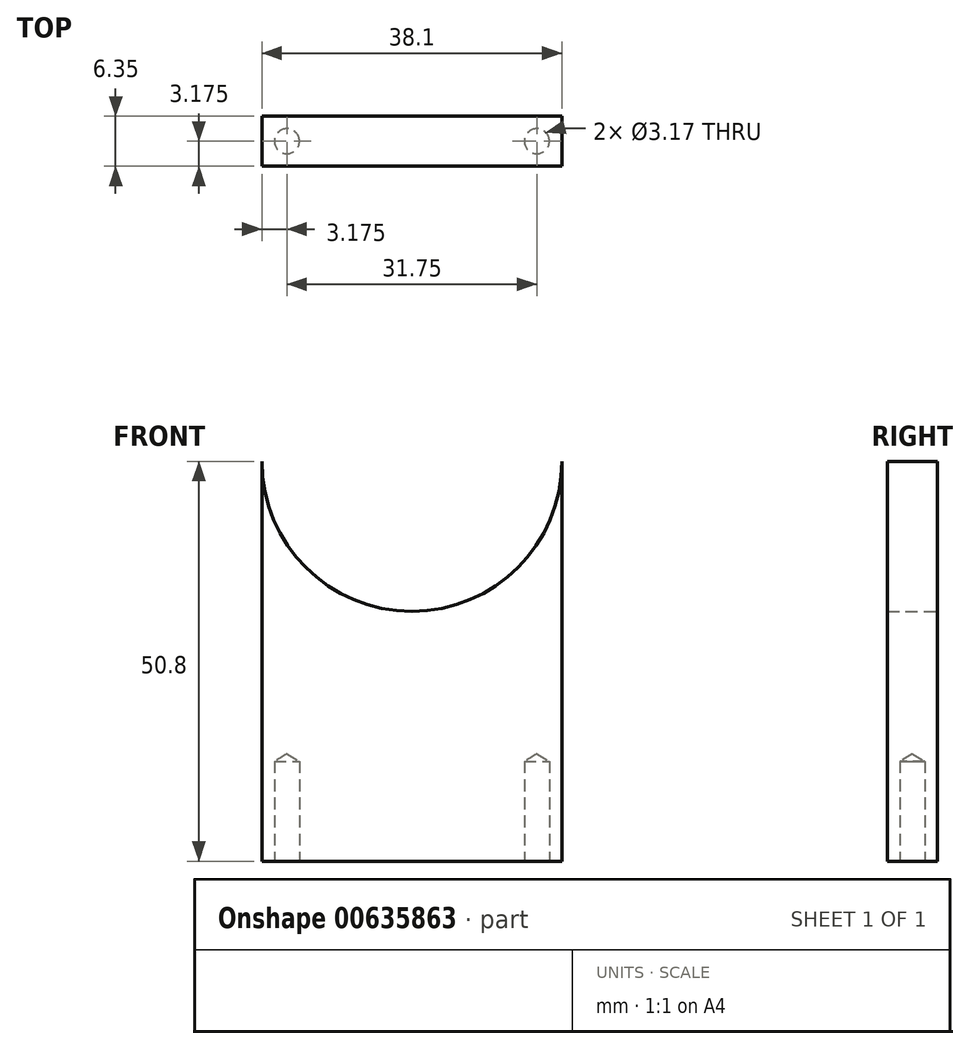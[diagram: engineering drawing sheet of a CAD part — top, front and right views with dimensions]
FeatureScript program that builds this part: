
annotation { "Feature Type Name" : "Feature", "Feature Type Description" : "" }
export const myFeature = defineFeature(function(context is Context, id is Id, definition is map)
    precondition{}
    {
        {
            var Q0;
            Q0=qCreatedBy(makeId("Front.planeOp"),FACE);
            var sketch = newSketch(context, id + "F0", { "sketchPlane" : qUnion([Q0])});
            skLineSegment(sketch, "E0.bottom", {"start": v(0, 0) * mm, "end": v(38.1, 0) * mm});
            skLineSegment(sketch, "E0.top", {"start": v(0, 50.8) * mm, "end": v(38.1, 50.8) * mm});
            skLineSegment(sketch, "E0.left", {"start": v(0, 0) * mm, "end": v(0, 50.8) * mm});
            skLineSegment(sketch, "E0.right", {"start": v(38.1, 0) * mm, "end": v(38.1, 50.8) * mm});
            skCircle(sketch, "E1", {"center": v(19.05, 50.8) * mm, "radius": 19.05 * mm});
            skSolve(sketch);
        }
        {
            var Q0;
            Q0=makeQuery(id+"F0.imprint","IMPRINT",FACE,{"disambiguationData":[TD([[makeQuery(id+"F0.imprint","IMPRINT",EDGE,{"derivedFrom":sQuery(id+"F0.wireOp",EDGE,"E0.bottom")}),1.0]])]});
            extrude(context, id + "F1", {"entities" : qUnion([Q0]), "depth" : 6.35 * mm, "offsetDistance" : 25.4 * mm});
        }
        {
            var Q0;
            Q0=makeQuery(id+"F1.opExtrude","SWEPT_FACE",FACE,{"disambiguationData":[OSD([sQuery(id+"F0.wireOp",EDGE,"E0.bottom")])]});
            var sketch = newSketch(context, id + "F2", { "sketchPlane" : qUnion([Q0])});
            skLineSegment(sketch, "E2", {"start": v(3.17, 6.35) * mm, "end": v(3.18, 0) * mm, "construction": true});
            skLineSegment(sketch, "E3", {"start": v(34.93, 6.35) * mm, "end": v(34.93, 0) * mm, "construction": true});
            skPoint(sketch, "E4", {"position": v(3.18, 3.18) * mm});
            skPoint(sketch, "E5", {"position": v(34.93, 3.18) * mm});
            skSolve(sketch);
        }
        {
            var Q0;
            Q0=sQuery(id+"F2.wireOp",VERTEX,"E4");
            var Q1;
            Q1=sQuery(id+"F2.wireOp",VERTEX,"E5");
            var Q2;
            Q2=makeQuery(id+"F1.opExtrude","SWEPT_BODY",BODY,{"disambiguationData":[OSD([sQuery(id+"F0.wireOp",EDGE,"E0.bottom"),sQuery(id+"F0.wireOp",EDGE,"E0.left"),sQuery(id+"F0.wireOp",EDGE,"E0.right"),sQuery(id+"F0.wireOp",EDGE,"E1")])]});
            hole(context, id + "F3", {"style" : HoleStyle.SIMPLE, "endStyle" : HoleEndStyle.BLIND, "holeDiameter" : 3.17 * mm, "majorDiameter" : 6.35 * mm, "holeDepth" : 12.7 * mm, "isTappedThrough" : true, "tappedDepth" : 12.7 * mm, "tapClearance" : 3, "locations" : qUnion([Q0, Q1]), "scope" : qUnion([Q2])});
        }
    });
